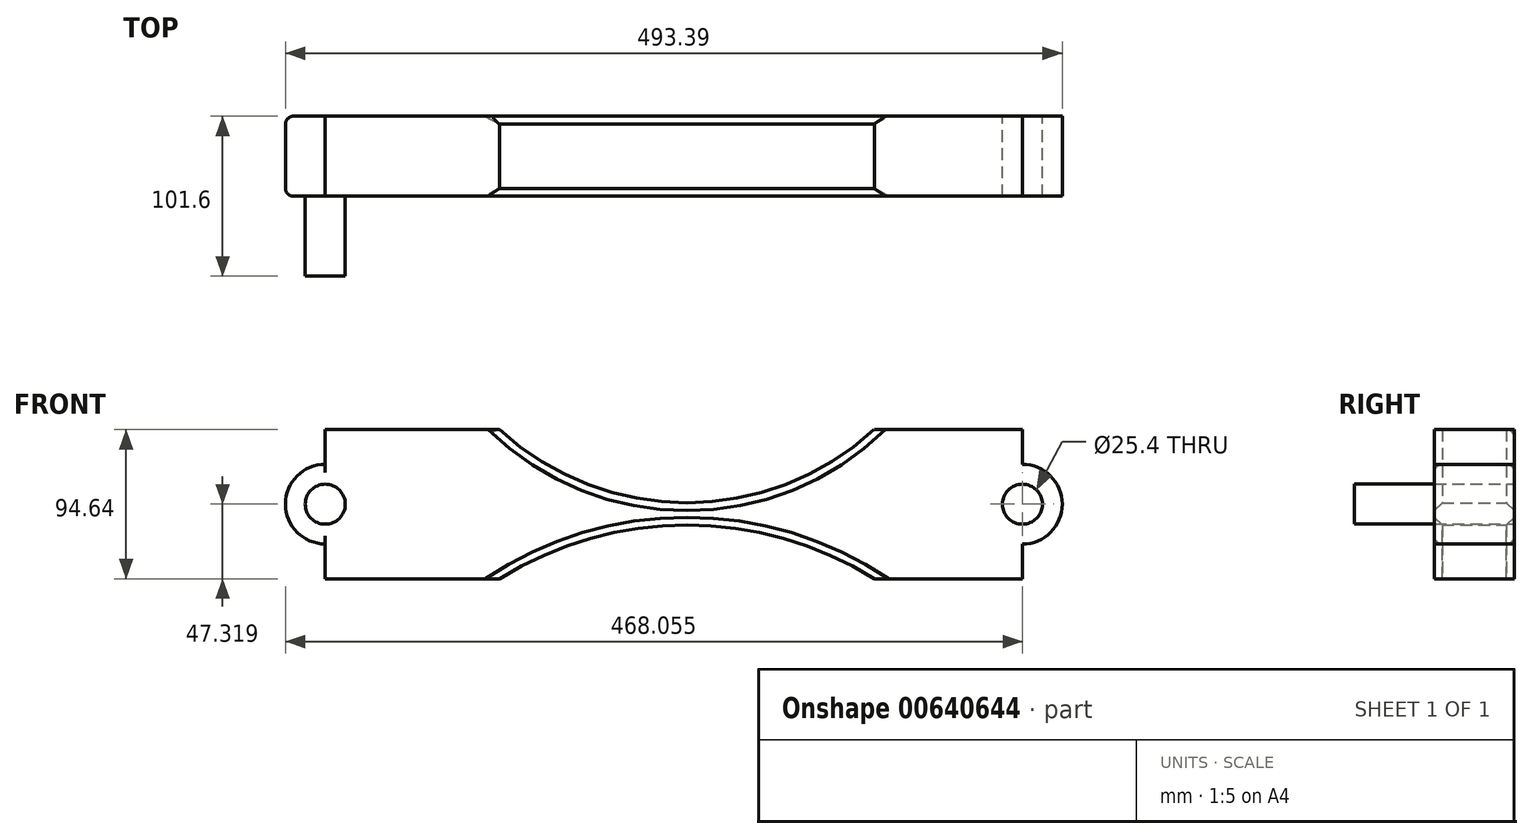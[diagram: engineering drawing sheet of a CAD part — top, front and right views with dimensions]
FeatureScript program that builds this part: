
annotation { "Feature Type Name" : "Feature", "Feature Type Description" : "" }
export const myFeature = defineFeature(function(context is Context, id is Id, definition is map)
    precondition{}
    {
        {
            var Q0;
            Q0=qCreatedBy(makeId("Front.planeOp"),FACE);
            var sketch = newSketch(context, id + "F0", { "sketchPlane" : qUnion([Q0])});
            skLineSegment(sketch, "E0.bottom", {"start": v(-192.23, 48.14) * mm, "end": v(-81.54, 48.14) * mm});
            skLineSegment(sketch, "E0.top", {"start": v(-192.23, -46.5) * mm, "end": v(-81.54, -46.5) * mm});
            skLineSegment(sketch, "E0.left", {"start": v(-192.23, 48.14) * mm, "end": v(-192.23, 13.52) * mm});
            skLineSegment(sketch, "E0.right", {"start": v(250.54, 48.14) * mm, "end": v(250.54, 13.52) * mm});
            skCircle(sketch, "E1", {"center": v(250.54, 0.82) * mm, "radius": 25.33 * mm});
            skCircle(sketch, "E2", {"center": v(-192.23, 0.82) * mm, "radius": 25.28 * mm});
            skCircle(sketch, "E3", {"center": v(250.54, 0.82) * mm, "radius": 12.7 * mm});
            skLineSegment(sketch, "E4.trimOffspring", {"start": v(250.54, -11.88) * mm, "end": v(250.54, -46.5) * mm});
            skCircle(sketch, "E5", {"center": v(-192.23, 0.82) * mm, "radius": 12.7 * mm});
            skLineSegment(sketch, "E6.trimOffspring", {"start": v(-192.23, -11.88) * mm, "end": v(-192.23, -46.5) * mm});
            skLineSegment(sketch, "E7", {"start": v(156.43, 48.14) * mm, "end": v(250.54, 48.14) * mm});
            skPoint(sketch, "E8", {"position": v(62.31, 48.14) * mm});
            skPoint(sketch, "E9", {"position": v(156.43, 48.14) * mm});
            skPoint(sketch, "E10", {"position": v(-81.54, 48.14) * mm});
            skArc(sketch, "E11", {"start": v(-81.54, 48.14) * mm, "mid": v(37.44, 1.72) * mm, "end": v(156.43, 48.14) * mm});
            skPoint(sketch, "E12.orphan", {"position": v(29.16, 48.14) * mm});
            skPoint(sketch, "E13", {"position": v(156.43, -46.5) * mm});
            skPoint(sketch, "E14", {"position": v(-81.54, -46.5) * mm});
            skLineSegment(sketch, "E15.trimOffspring", {"start": v(156.43, -46.5) * mm, "end": v(250.54, -46.5) * mm});
            skArc(sketch, "E16", {"start": v(156.43, -46.5) * mm, "mid": v(37.44, -12.49) * mm, "end": v(-81.54, -46.5) * mm});
            skSolve(sketch);
        }
        {
            var Q0;
            Q0=makeQuery(id+"F0.imprint","IMPRINT",FACE,{"disambiguationData":[TD([[makeQuery(id+"F0.imprint","IMPRINT",EDGE,{"derivedFrom":sQuery(id+"F0.wireOp",EDGE,"E0.bottom")}),-1.0]])]});
            extrude(context, id + "F1", {"entities" : qUnion([Q0]), "depth" : 50.8 * mm});
        }
        {
            var Q0;
            Q0=qSketchRegion(id+"F0",true);
            extrude(context, id + "F2", {"entities" : qUnion([Q0]), "operationType" : NewBodyOperationType.ADD, "depth" : 50.8 * mm});
        }
        {
            var Q0;
            Q0=qSketchRegion(id+"F0",true);
            extrude(context, id + "F3", {"entities" : qUnion([Q0]), "operationType" : NewBodyOperationType.ADD, "depth" : 25.4 * mm});
        }
        {
            var Q0;
            {var subQ0=sQuery(id+"F0.wireOp",EDGE,"E5");var subQ2=makeQuery(id+"F0.imprint","INTERSECT",VERTEX,{"derivedFrom":[sQuery(id+"F0.wireOp",EDGE,"E0.left"),subQ0]});Q0=makeQuery(id+"F0.imprint","IMPRINT",FACE,{"disambiguationData":[TD([[makeQuery(id+"F0.imprint","IMPRINT",EDGE,{"disambiguationData":[TD([[subQ2,-1.0]])],"derivedFrom":subQ0}),1.0]])]});}
            extrude(context, id + "F4", {"entities" : qUnion([Q0]), "operationType" : NewBodyOperationType.ADD, "depth" : 101.6 * mm});
        }
        {
            var Q0;
            Q0=makeQuery(id+"F1.opExtrude","CAP_EDGE",EDGE,{"disambiguationData":[OSD([sQuery(id+"F0.wireOp",EDGE,"E11")])],"isStart":true});
            var Q1;
            Q1=makeQuery(id+"F1.opExtrude","CAP_EDGE",EDGE,{"disambiguationData":[OSD([sQuery(id+"F0.wireOp",EDGE,"E16")])],"isStart":true});
            var Q2;
            Q2=makeQuery(id+"F1.opExtrude","CAP_EDGE",EDGE,{"disambiguationData":[OSD([sQuery(id+"F0.wireOp",EDGE,"E11")])],"isStart":false});
            var Q3;
            Q3=makeQuery(id+"F1.opExtrude","CAP_EDGE",EDGE,{"disambiguationData":[OSD([sQuery(id+"F0.wireOp",EDGE,"E16")])],"isStart":false});
            chamfer(context, id + "F5", {"entities" : qUnion([Q0, Q1, Q2, Q3]), "width" : 5 * mm, "tangentPropagation" : true});
        }
        {
            var Q0;
            Q0=makeQuery(id+"F1.opExtrude","CAP_EDGE",EDGE,{"disambiguationData":[OSD([sQuery(id+"F0.wireOp",EDGE,"E11")])],"isStart":true});
            var Q1;
            Q1=makeQuery(id+"F1.opExtrude","CAP_EDGE",EDGE,{"disambiguationData":[OSD([sQuery(id+"F0.wireOp",EDGE,"E16")])],"isStart":true});
            var Q2;
            Q2=makeQuery(id+"F1.opExtrude","CAP_EDGE",EDGE,{"disambiguationData":[OSD([sQuery(id+"F0.wireOp",EDGE,"E0.bottom")])],"isStart":true});
            var Q3;
            Q3=makeQuery(id+"F2.opExtrude","CAP_EDGE",EDGE,{"disambiguationData":[OSD([sQuery(id+"F0.wireOp",EDGE,"E2")])],"isStart":true});
            var Q4;
            Q4=makeQuery(id+"F2.opExtrude","CAP_EDGE",EDGE,{"disambiguationData":[OSD([sQuery(id+"F0.wireOp",EDGE,"E2")])],"isStart":false});
            fillet(context, id + "F6", {"entities" : qUnion([Q0, Q1, Q2, Q3, Q4]), "radius" : 5 * mm, "tangentPropagation" : true, "allowEdgeOverflow" : false});
        }
    });
